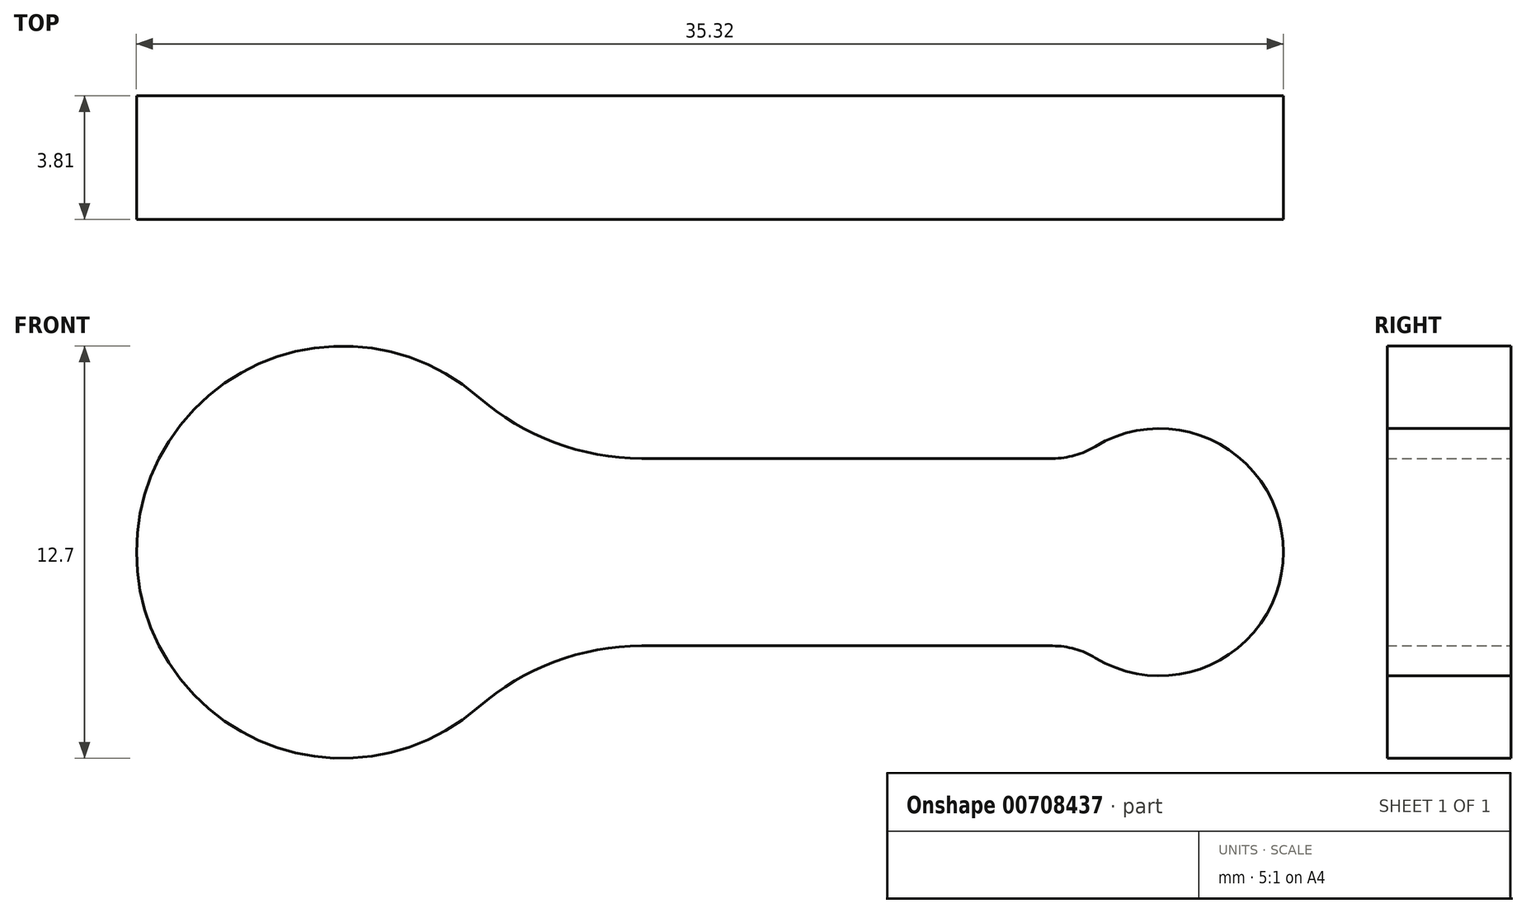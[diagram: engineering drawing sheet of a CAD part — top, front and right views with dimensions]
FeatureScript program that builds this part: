
annotation { "Feature Type Name" : "Feature", "Feature Type Description" : "" }
export const myFeature = defineFeature(function(context is Context, id is Id, definition is map)
    precondition{}
    {
        {
            var Q0;
            Q0=qCreatedBy(makeId("Front.planeOp"),FACE);
            var sketch = newSketch(context, id + "F0", { "sketchPlane" : qUnion([Q0])});
            skArc(sketch, "E0", {"start": v(-11.9, 4.78) * mm, "mid": v(-22.44, 0) * mm, "end": v(-11.9, -4.78) * mm});
            skArc(sketch, "E1", {"start": v(7.1, -3.26) * mm, "mid": v(12.88, 0) * mm, "end": v(7.1, 3.26) * mm});
            skLineSegment(sketch, "E2.bottom", {"start": v(-6.88, -2.89) * mm, "end": v(5.78, -2.89) * mm});
            skLineSegment(sketch, "E2.top", {"start": v(-6.88, 2.89) * mm, "end": v(5.78, 2.89) * mm});
            skPoint(sketch, "E3.visualSharp", {"position": v(6.59, 2.89) * mm});
            skArc(sketch, "E3.filletArc", {"start": v(5.78, 2.89) * mm, "mid": v(6.46, 2.98) * mm, "end": v(7.1, 3.26) * mm});
            skPoint(sketch, "E4.visualSharp", {"position": v(6.59, -2.89) * mm});
            skArc(sketch, "E4.filletArc", {"start": v(7.1, -3.26) * mm, "mid": v(6.46, -2.98) * mm, "end": v(5.78, -2.89) * mm});
            skPoint(sketch, "E5.visualSharp", {"position": v(-10.43, 2.89) * mm});
            skArc(sketch, "E5.filletArc", {"start": v(-11.9, 4.78) * mm, "mid": v(-9.56, 3.38) * mm, "end": v(-6.88, 2.89) * mm});
            skPoint(sketch, "E6.visualSharp", {"position": v(-10.43, -2.89) * mm});
            skArc(sketch, "E6.filletArc", {"start": v(-6.88, -2.89) * mm, "mid": v(-9.56, -3.38) * mm, "end": v(-11.9, -4.78) * mm});
            skCircle(sketch, "E7", {"center": v(-16.09, 0) * mm, "radius": 5.08 * mm});
            skCircle(sketch, "E8", {"center": v(9.07, 0) * mm, "radius": 2.54 * mm});
            skSolve(sketch);
        }
        {
            var Q0;
            Q0=makeQuery(id+"F0.imprint","IMPRINT",FACE,{"disambiguationData":[TD([[makeQuery(id+"F0.imprint","IMPRINT",EDGE,{"derivedFrom":sQuery(id+"F0.wireOp",EDGE,"E0")}),1.0]])]});
            var Q1;
            Q1=makeQuery(id+"F0.imprint","IMPRINT",FACE,{"disambiguationData":[TD([[makeQuery(id+"F0.imprint","IMPRINT",EDGE,{"derivedFrom":sQuery(id+"F0.wireOp",EDGE,"E7")}),1.0]])]});
            var Q2;
            Q2=makeQuery(id+"F0.imprint","IMPRINT",FACE,{"disambiguationData":[TD([[makeQuery(id+"F0.imprint","IMPRINT",EDGE,{"derivedFrom":sQuery(id+"F0.wireOp",EDGE,"E8")}),1.0]])]});
            extrude(context, id + "F1", {"entities" : qUnion([Q0, Q1, Q2]), "depth" : 3.8 * mm, "offsetDistance" : 25.4 * mm});
        }
    });
